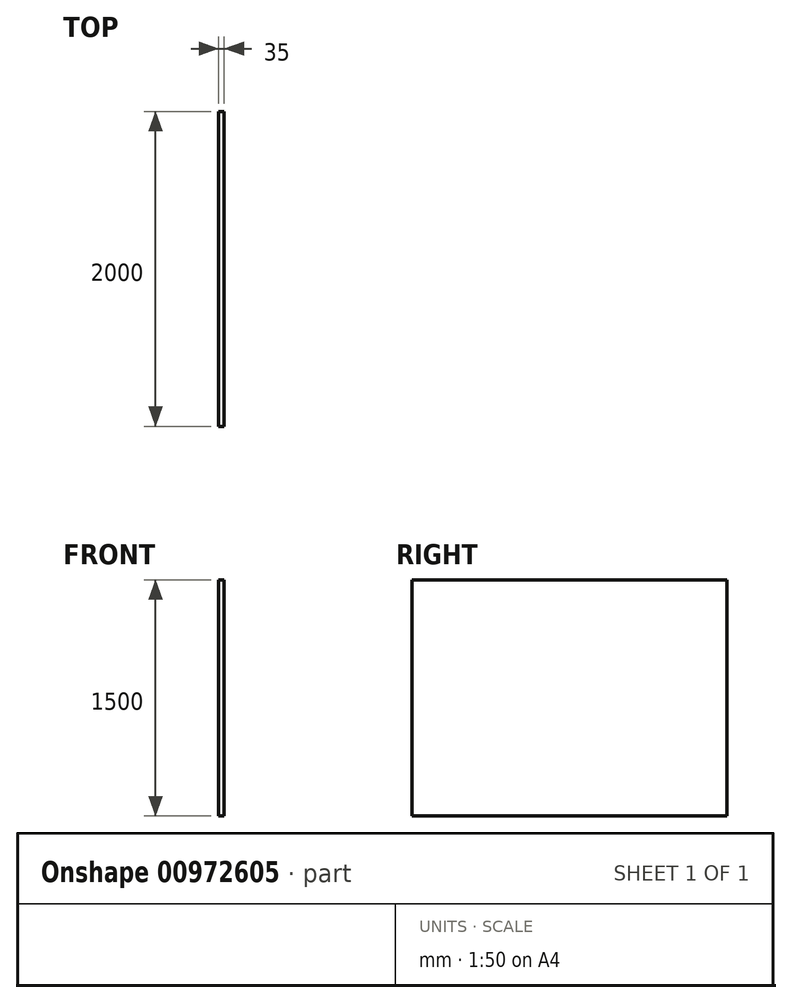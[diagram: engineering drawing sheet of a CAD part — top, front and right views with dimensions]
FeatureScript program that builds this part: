
annotation { "Feature Type Name" : "Feature", "Feature Type Description" : "" }
export const myFeature = defineFeature(function(context is Context, id is Id, definition is map)
    precondition{}
    {
        {
            var Q0;
            Q0=qCreatedBy(makeId("Right.planeOp"),FACE);
            var sketch = newSketch(context, id + "F0", { "sketchPlane" : qUnion([Q0])});
            skLineSegment(sketch, "E0.bottom", {"start": v(0, 0) * mm, "end": v(2000, 0) * mm});
            skLineSegment(sketch, "E0.top", {"start": v(0, 1500) * mm, "end": v(2000, 1500) * mm});
            skLineSegment(sketch, "E0.left", {"start": v(0, 0) * mm, "end": v(0, 1500) * mm});
            skLineSegment(sketch, "E0.right", {"start": v(2000, 0) * mm, "end": v(2000, 1500) * mm});
            skSolve(sketch);
        }
        {
            var Q0;
            Q0=makeQuery(id+"F0.imprint","IMPRINT",FACE,{"disambiguationData":[TD([[makeQuery(id+"F0.imprint","IMPRINT",EDGE,{"derivedFrom":sQuery(id+"F0.wireOp",EDGE,"E0.bottom")}),1.0]])]});
            extrude(context, id + "F1", {"entities" : qUnion([Q0]), "depth" : 35 * mm, "offsetDistance" : 25 * mm});
        }
    });
